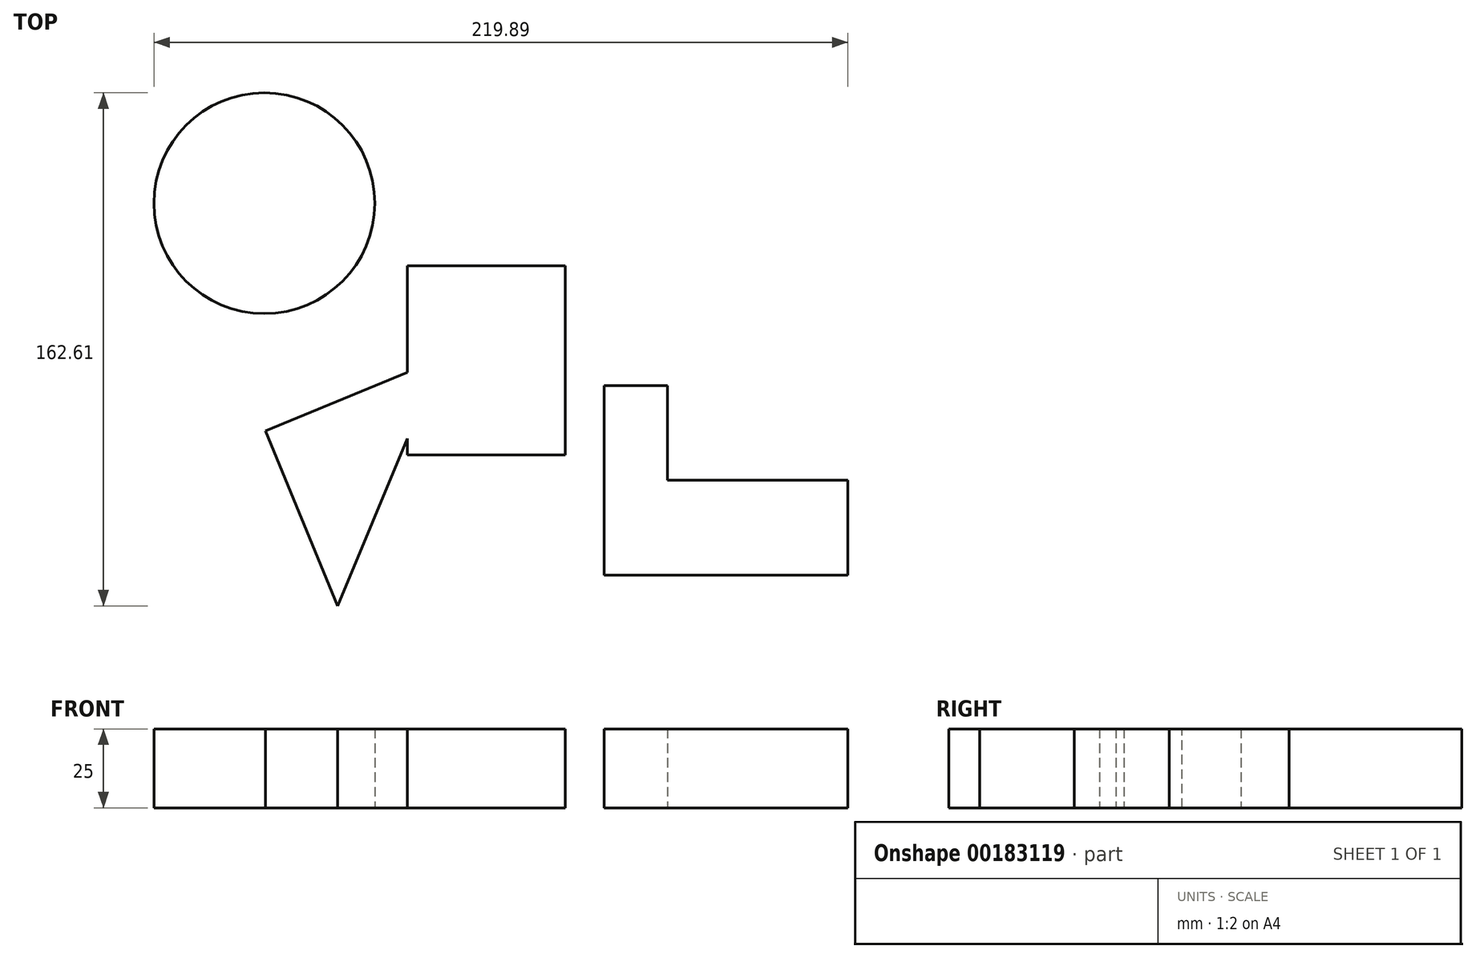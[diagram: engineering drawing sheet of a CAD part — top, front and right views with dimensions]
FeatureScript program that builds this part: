
annotation { "Feature Type Name" : "Feature", "Feature Type Description" : "" }
export const myFeature = defineFeature(function(context is Context, id is Id, definition is map)
    precondition{}
    {
        {
            var Q0;
            Q0=qCreatedBy(makeId("Top.planeOp"),FACE);
            var sketch = newSketch(context, id + "F0", { "sketchPlane" : qUnion([Q0])});
            skLineSegment(sketch, "E0.bottom", {"start": v(-18.4, 38.33) * mm, "end": v(31.6, 38.33) * mm});
            skLineSegment(sketch, "E0.top", {"start": v(-18.4, -21.67) * mm, "end": v(31.6, -21.67) * mm});
            skLineSegment(sketch, "E0.left", {"start": v(-18.4, 38.33) * mm, "end": v(-18.4, -21.67) * mm});
            skLineSegment(sketch, "E0.right", {"start": v(31.6, 38.33) * mm, "end": v(31.6, -21.67) * mm});
            skSolve(sketch);
        }
        {
            var Q0;
            Q0=qCreatedBy(makeId("Top.planeOp"),FACE);
            var sketch = newSketch(context, id + "F1", { "sketchPlane" : qUnion([Q0])});
            skLineSegment(sketch, "E1.0", {"start": v(-40.53, -69.49) * mm, "end": v(-63.34, -14) * mm});
            skLineSegment(sketch, "E1.1", {"start": v(-63.34, -14) * mm, "end": v(-7.85, 8.81) * mm});
            skLineSegment(sketch, "E1.2", {"start": v(-7.85, 8.81) * mm, "end": v(-40.53, -69.49) * mm});
            skPoint(sketch, "E1.0.midPoint", {"position": v(-51.94, -41.74) * mm});
            skSolve(sketch);
        }
        {
            var Q0;
            Q0=qCreatedBy(makeId("Top.planeOp"),FACE);
            var sketch = newSketch(context, id + "F2", { "sketchPlane" : qUnion([Q0])});
            skCircle(sketch, "E2", {"center": v(-63.76, 58.12) * mm, "radius": 35 * mm});
            skSolve(sketch);
        }
        {
            var Q0;
            Q0=qCreatedBy(makeId("Top.planeOp"),FACE);
            var sketch = newSketch(context, id + "F3", { "sketchPlane" : qUnion([Q0])});
            skLineSegment(sketch, "E3.bottom", {"start": v(43.92, 0.3) * mm, "end": v(63.92, 0.3) * mm});
            skLineSegment(sketch, "E3.top", {"start": v(43.92, -59.7) * mm, "end": v(63.92, -59.7) * mm});
            skLineSegment(sketch, "E3.left", {"start": v(43.92, 0.3) * mm, "end": v(43.92, -59.7) * mm});
            skLineSegment(sketch, "E3.right", {"start": v(63.92, 0.3) * mm, "end": v(63.92, -29.7) * mm});
            skLineSegment(sketch, "E4.bottom", {"start": v(63.92, -29.7) * mm, "end": v(121.13, -29.7) * mm});
            skLineSegment(sketch, "E4.top", {"start": v(61.13, -59.7) * mm, "end": v(121.13, -59.7) * mm});
            skLineSegment(sketch, "E4.right", {"start": v(121.13, -29.7) * mm, "end": v(121.13, -59.7) * mm});
            skSolve(sketch);
        }
        {
            var Q0;
            Q0=makeQuery(id+"F2.imprint","IMPRINT",FACE,{"disambiguationData":[TD([[makeQuery(id+"F2.imprint","IMPRINT",EDGE,{"derivedFrom":sQuery(id+"F2.wireOp",EDGE,"E2")}),1.0]])]});
            extrude(context, id + "F4", {"entities" : qUnion([Q0]), "depth" : 25 * mm});
        }
        {
            var Q0;
            Q0=makeQuery(id+"F0.imprint","IMPRINT",FACE,{"disambiguationData":[TD([[makeQuery(id+"F0.imprint","IMPRINT",EDGE,{"derivedFrom":sQuery(id+"F0.wireOp",EDGE,"E0.bottom")}),-1.0]])]});
            extrude(context, id + "F5", {"entities" : qUnion([Q0]), "depth" : 25 * mm});
        }
        {
            var Q0;
            Q0=makeQuery(id+"F1.imprint","IMPRINT",FACE,{"disambiguationData":[TD([[makeQuery(id+"F1.imprint","IMPRINT",EDGE,{"derivedFrom":sQuery(id+"F1.wireOp",EDGE,"E1.0")}),-1.0]])]});
            extrude(context, id + "F6", {"entities" : qUnion([Q0]), "operationType" : NewBodyOperationType.ADD, "depth" : 25 * mm});
        }
        {
            var Q0;
            Q0=makeQuery(id+"F3.imprint","IMPRINT",FACE,{"disambiguationData":[TD([[makeQuery(id+"F3.imprint","IMPRINT",EDGE,{"derivedFrom":sQuery(id+"F3.wireOp",EDGE,"E3.bottom")}),-1.0]])]});
            extrude(context, id + "F7", {"entities" : qUnion([Q0]), "depth" : 25 * mm});
        }
    });
